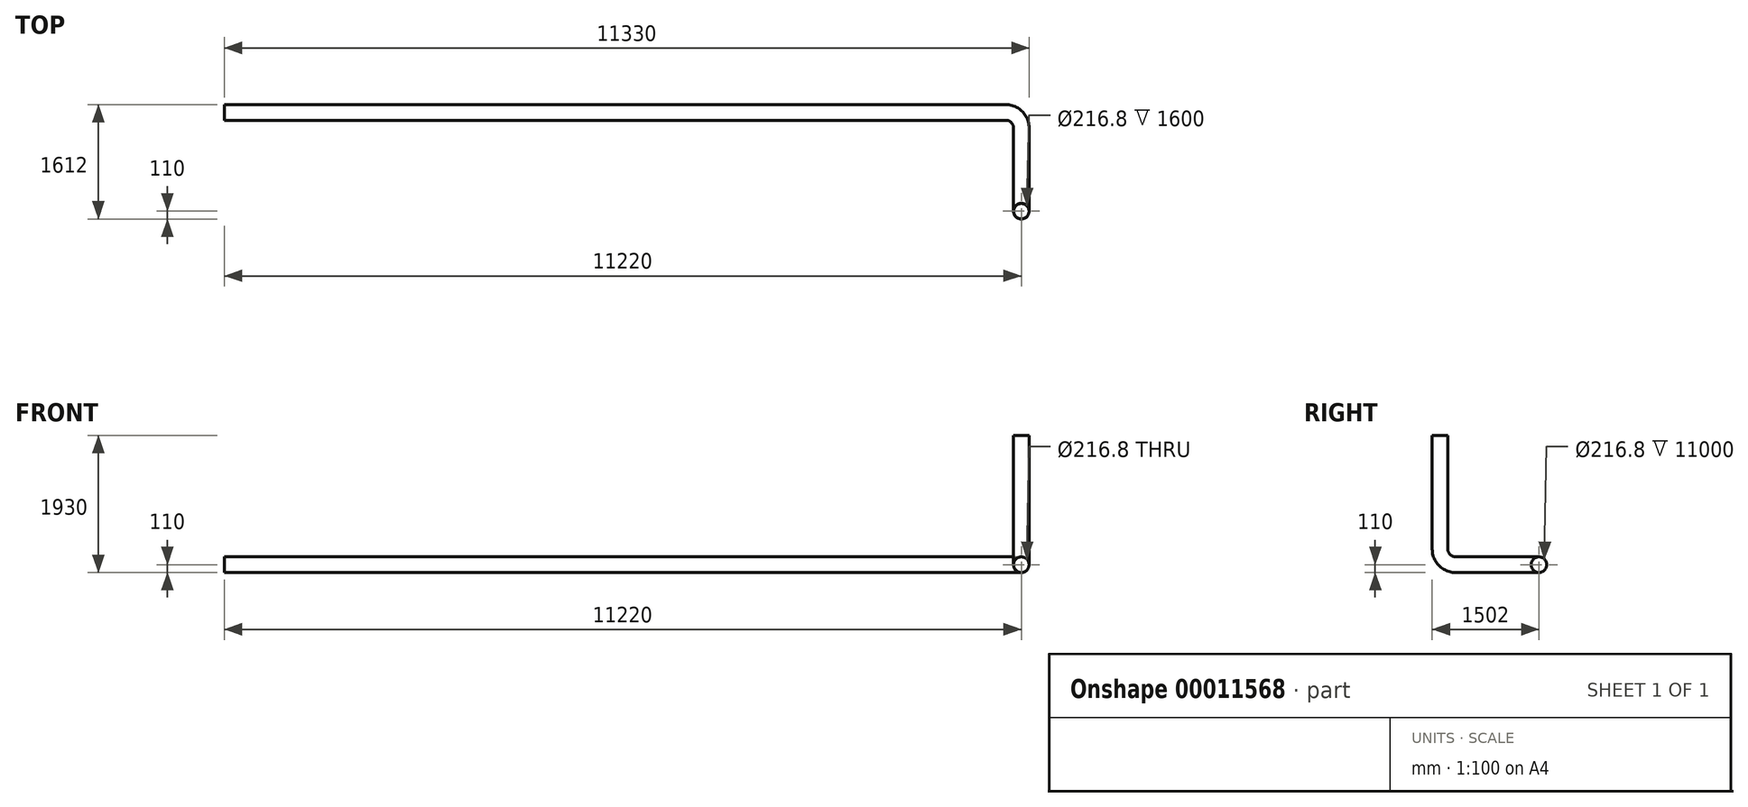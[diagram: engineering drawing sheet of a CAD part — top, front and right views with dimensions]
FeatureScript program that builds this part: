
annotation { "Feature Type Name" : "Feature", "Feature Type Description" : "" }
export const myFeature = defineFeature(function(context is Context, id is Id, definition is map)
    precondition{}
    {
        {
            var Q0;
            Q0=qCreatedBy(makeId("Top.planeOp"),FACE);
            cPlane(context, id + "F0", {"entities" : qUnion([Q0]), "cplaneType" : CPlaneType.OFFSET, "offset" : 1820 * mm, "oppositeDirection" : true, "width" : 150 * mm, "height" : 150 * mm});
        }
        {
            var Q0;
            Q0=qCreatedBy(makeId("Top.planeOp"),FACE);
            var sketch = newSketch(context, id + "F1", { "sketchPlane" : qUnion([Q0])});
            skCircle(sketch, "E0", {"center": v(0, 0) * mm, "radius": 110 * mm});
            skSolve(sketch);
        }
        {
            var Q0;
            Q0=qCreatedBy(makeId("Right.planeOp"),FACE);
            var sketch = newSketch(context, id + "F2", { "sketchPlane" : qUnion([Q0])});
            skLineSegment(sketch, "E1", {"start": v(0, 0) * mm, "end": v(0, -1600) * mm});
            skLineSegment(sketch, "E2", {"start": v(220, -1820) * mm, "end": v(1172, -1820) * mm});
            skArc(sketch, "E3.filletArc", {"start": v(0, -1600) * mm, "mid": v(64.44, -1755.56) * mm, "end": v(220, -1820) * mm});
            skSolve(sketch);
        }
        {
            var Q0;
            Q0=qCreatedBy(id+"F0.planeOp",FACE);
            var sketch = newSketch(context, id + "F3", { "sketchPlane" : qUnion([Q0])});
            skLineSegment(sketch, "E4", {"start": v(-220, 1392) * mm, "end": v(-11220, 1392) * mm});
            skLineSegment(sketch, "E5", {"start": v(0, 1172) * mm, "end": v(0, 1172) * mm});
            skPoint(sketch, "E6.visualSharp", {"position": v(0, 1392) * mm});
            skArc(sketch, "E6.filletArc", {"start": v(0, 1172) * mm, "mid": v(-64.44, 1327.56) * mm, "end": v(-220, 1392) * mm});
            skSolve(sketch);
        }
        {
            var Q0;
            Q0 = qSketchRegion(id + "F1", true);
            var Q1;
            Q1 = qBodyType(qCreatedBy(id + "F3" ,EDGE), BodyType.WIRE);
            var Q2;
            Q2 = qBodyType(qCreatedBy(id + "F2" ,EDGE), BodyType.WIRE);
            sweep(context, id + "F4", {"profiles" : qUnion([Q0]), "path" : qUnion([Q1, Q2])});
        }
        {
            var Q0;
            Q0=makeQuery(id+"F4.opSweep","CAP_FACE",FACE,{"disambiguationData":[OSD([sQuery(id+"FwigS6PKJAqavTk_0.wireOp",VERTEX,"01974570-1cdc-4aa1-826b-aab295ef268f.start"),sQuery(id+"F1.wireOp",EDGE,"E0")])],"isStart":true});
            var Q1;
            Q1=makeQuery(id+"F4.opSweep","CAP_FACE",FACE,{"disambiguationData":[OSD([sQuery(id+"F3.wireOp",VERTEX,"d53e4fb0-5c29-402d-b917-070d6dde65fe.end"),sQuery(id+"F1.wireOp",EDGE,"E0")])],"isStart":false});
            shell(context, id + "F5", {"entities" : qUnion([Q0, Q1]), "thickness" : 1.6 * mm});
        }
    });
